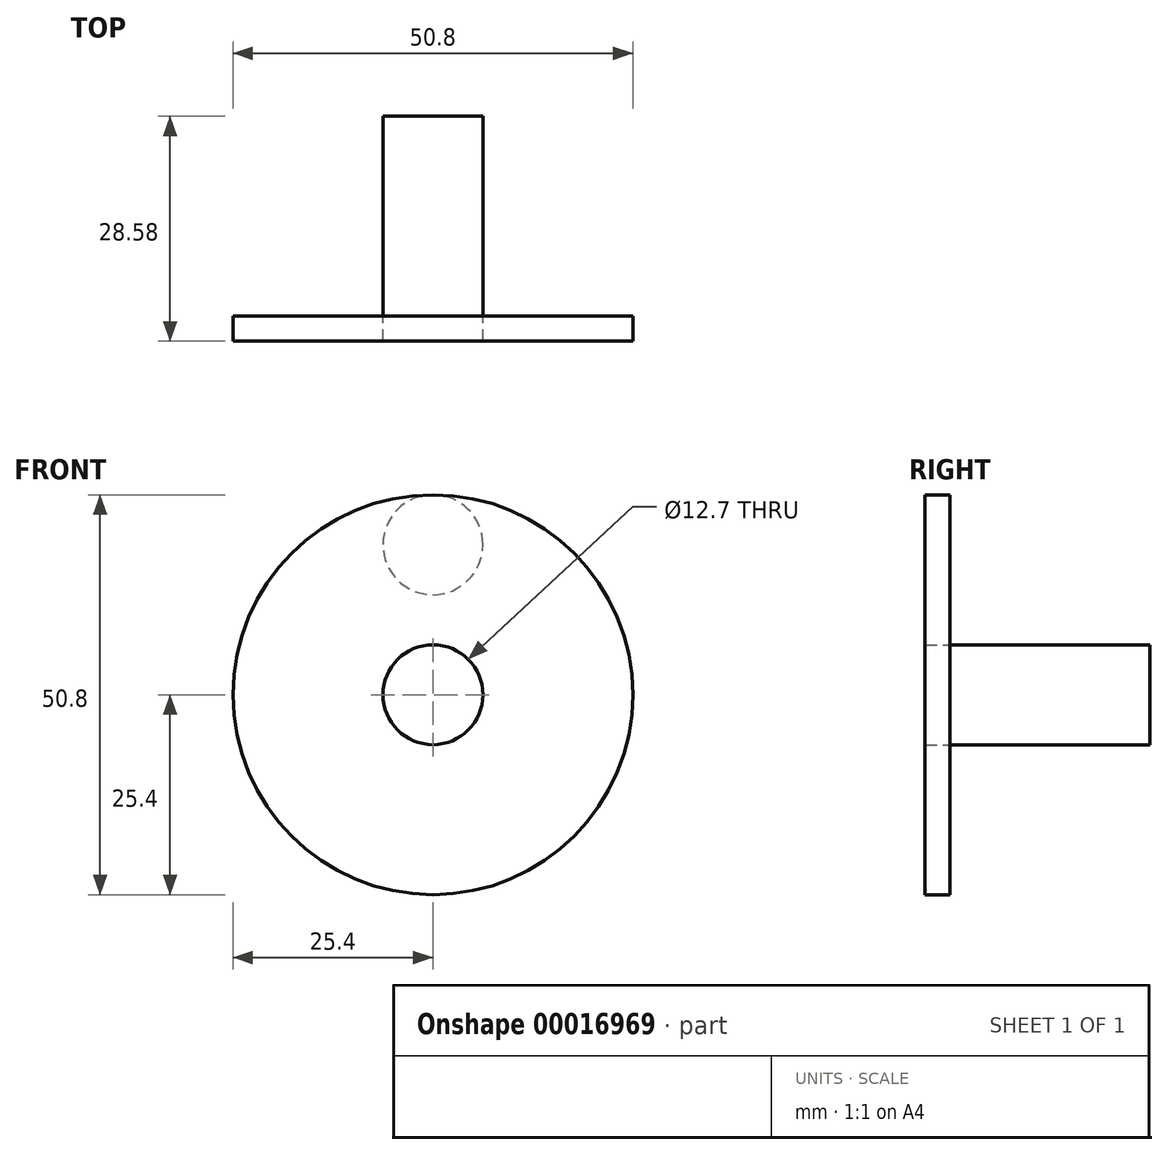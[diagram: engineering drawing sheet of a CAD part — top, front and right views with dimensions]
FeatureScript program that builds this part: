
annotation { "Feature Type Name" : "Feature", "Feature Type Description" : "" }
export const myFeature = defineFeature(function(context is Context, id is Id, definition is map)
    precondition{}
    {
        {
            var Q0;
            Q0=qCreatedBy(makeId("Front.planeOp"),FACE);
            var sketch = newSketch(context, id + "F0", { "sketchPlane" : qUnion([Q0])});
            skCircle(sketch, "E0", {"center": v(0, 0) * mm, "radius": 6.35 * mm});
            skSolve(sketch);
        }
        {
            var Q0;
            Q0=qCreatedBy(makeId("Front.planeOp"),FACE);
            var sketch = newSketch(context, id + "F1", { "sketchPlane" : qUnion([Q0])});
            skCircle(sketch, "E1", {"center": v(0, 0) * mm, "radius": 6.35 * mm});
            skCircle(sketch, "E2", {"center": v(0, 0) * mm, "radius": 25.4 * mm});
            skCircle(sketch, "E3", {"center": v(0, 19.05) * mm, "radius": 6.35 * mm});
            skSolve(sketch);
        }
        {
            var Q0;
            Q0 = qSketchRegion(id + "F0", true);
            extrude(context, id + "F2", {"entities" : qUnion([Q0]), "oppositeDirection" : true, "depth" : 25.4 * mm});
        }
        {
            var Q0;
            Q0=makeQuery(id+"F1.imprint","IMPRINT",FACE,{"disambiguationData":[TD([[makeQuery(id+"F1.imprint","IMPRINT",EDGE,{"derivedFrom":sQuery(id+"F1.wireOp",EDGE,"E3")}),1.0]])]});
            extrude(context, id + "F3", {"entities" : qUnion([Q0]), "depth" : 1 / 101.6 * mm});
        }
        {
            var Q0;
            Q0 = qSketchRegion(id + "F1", true);
            var Q1;
            Q1=makeQuery(id+"F1.imprint","IMPRINT",FACE,{"disambiguationData":[TD([[makeQuery(id+"F1.imprint","IMPRINT",EDGE,{"derivedFrom":sQuery(id+"F1.wireOp",EDGE,"E3")}),1.0]])]});
            extrude(context, id + "F4", {"entities" : qUnion([Q0, Q1]), "depth" : 3.17 * mm});
        }
    });
